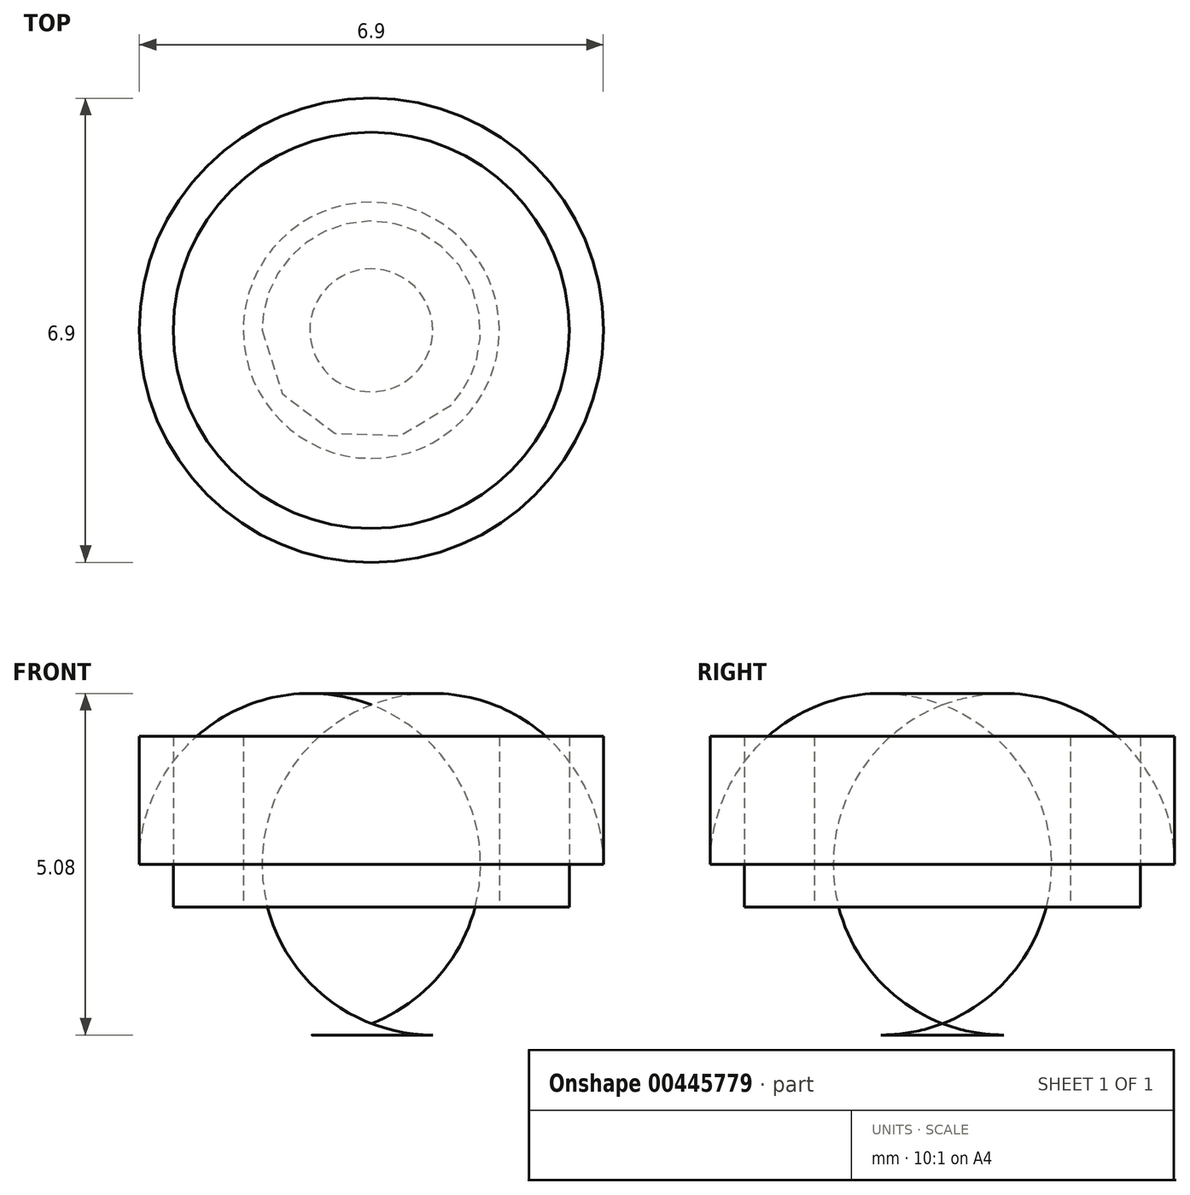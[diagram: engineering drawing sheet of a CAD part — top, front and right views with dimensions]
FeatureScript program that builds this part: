
annotation { "Feature Type Name" : "Feature", "Feature Type Description" : "" }
export const myFeature = defineFeature(function(context is Context, id is Id, definition is map)
    precondition{}
    {
        {
            var Q0;
            Q0=qCreatedBy(makeId("Top.planeOp"),FACE);
            var sketch = newSketch(context, id + "F0", { "sketchPlane" : qUnion([Q0])});
            skCircle(sketch, "E0", {"center": v(0, 0) * mm, "radius": 3.45 * mm});
            skCircle(sketch, "E1", {"center": v(0, 0) * mm, "radius": 2.95 * mm});
            skSolve(sketch);
        }
        {
            var Q0;
            Q0=makeQuery(id+"F0.imprint","IMPRINT",FACE,{"disambiguationData":[TD([[makeQuery(id+"F0.imprint","IMPRINT",EDGE,{"derivedFrom":sQuery(id+"F0.wireOp",EDGE,"E1")}),-1.0]])]});
            extrude(context, id + "F1", {"entities" : qUnion([Q0]), "depth" : 4.44 * mm});
        }
        {
            var Q0;
            Q0=makeQuery(id+"F0.imprint","IMPRINT",FACE,{"disambiguationData":[TD([[makeQuery(id+"F0.imprint","IMPRINT",EDGE,{"derivedFrom":sQuery(id+"F0.wireOp",EDGE,"E1")}),-1.0]])]});
            var Q1;
            Q1=makeQuery(id+"F0.imprint","IMPRINT",FACE,{"disambiguationData":[TD([[makeQuery(id+"F0.imprint","IMPRINT",EDGE,{"derivedFrom":sQuery(id+"F0.wireOp",EDGE,"E1")}),1.0]])]});
            extrude(context, id + "F2", {"entities" : qUnion([Q0, Q1]), "operationType" : NewBodyOperationType.ADD, "depth" : 1.9 * mm});
        }
        {
            var Q0;
            Q0=makeQuery(id+"F2.opExtrude","CAP_FACE",FACE,{"disambiguationData":[OSD([sQuery(id+"F0.wireOp",EDGE,"E0")])],"isStart":false});
            var sketch = newSketch(context, id + "F3", { "sketchPlane" : qUnion([Q0])});
            skCircle(sketch, "E2", {"center": v(0, 0) * mm, "radius": 1.9 * mm});
            skSolve(sketch);
        }
        {
            var Q0;
            Q0=makeQuery(id+"F3.imprint","IMPRINT",FACE,{"disambiguationData":[TD([[makeQuery(id+"F3.imprint","IMPRINT",EDGE,{"derivedFrom":sQuery(id+"F3.wireOp",EDGE,"E2")}),1.0]])]});
            extrude(context, id + "F4", {"entities" : qUnion([Q0]), "operationType" : NewBodyOperationType.ADD, "depth" : 2.54 * mm});
        }
        {
            var Q0;
            Q0=makeQuery(id+"F1.opExtrude","CAP_EDGE",EDGE,{"disambiguationData":[OSD([sQuery(id+"F0.wireOp",EDGE,"E0")])],"isStart":true});
            fillet(context, id + "F5", {"entities" : qUnion([Q0]), "radius" : 2.54 * mm, "tangentPropagation" : true, "allowEdgeOverflow" : false});
        }
    });
